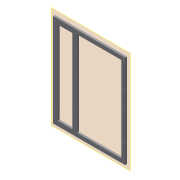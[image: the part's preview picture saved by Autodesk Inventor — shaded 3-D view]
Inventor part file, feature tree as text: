
AUTODESK INVENTOR PART (.ipt)
format: ipt  version: 2019.4 (Build 234330000, 330)  size: 126,464 bytes
history: native  units: mm
features: other x3, plane x1, extrude x1, hole x1, sketch x1
ambient origin geometry x8: Origin, YZ Plane, XZ Plane, XY Plane, X Axis, Y Axis, Z Axis, Center Point
bodies: Body1 (feature_tree)
feature tree (7):
  plane  "Work Plane3"
  extrude  "Extrusion3"  [1 undecoded]
  hole  "Hole2"  [1 undecoded]
  sketch  "Sketch6"  dims[d11=5.0mm d12=0.0mm d13=2.8mm d14=6.0mm d15=4.0mm d16=2.0mm d17=90.0deg d18=8.0mm d19=20.594885mm]
  other  "Assembly_Opentrons_Imagingunit_v3.iam"
  other  "Assembly_opentrons_microscope_slide_y_base:1"
  other  "02_Opentrons_Microscope_Base_v0:1"
note: 2 required parameter values undecoded (feature->parameter linkage not recoverable at this tier; creation-order binding heuristic only, values carry confidence <= 0.55)
